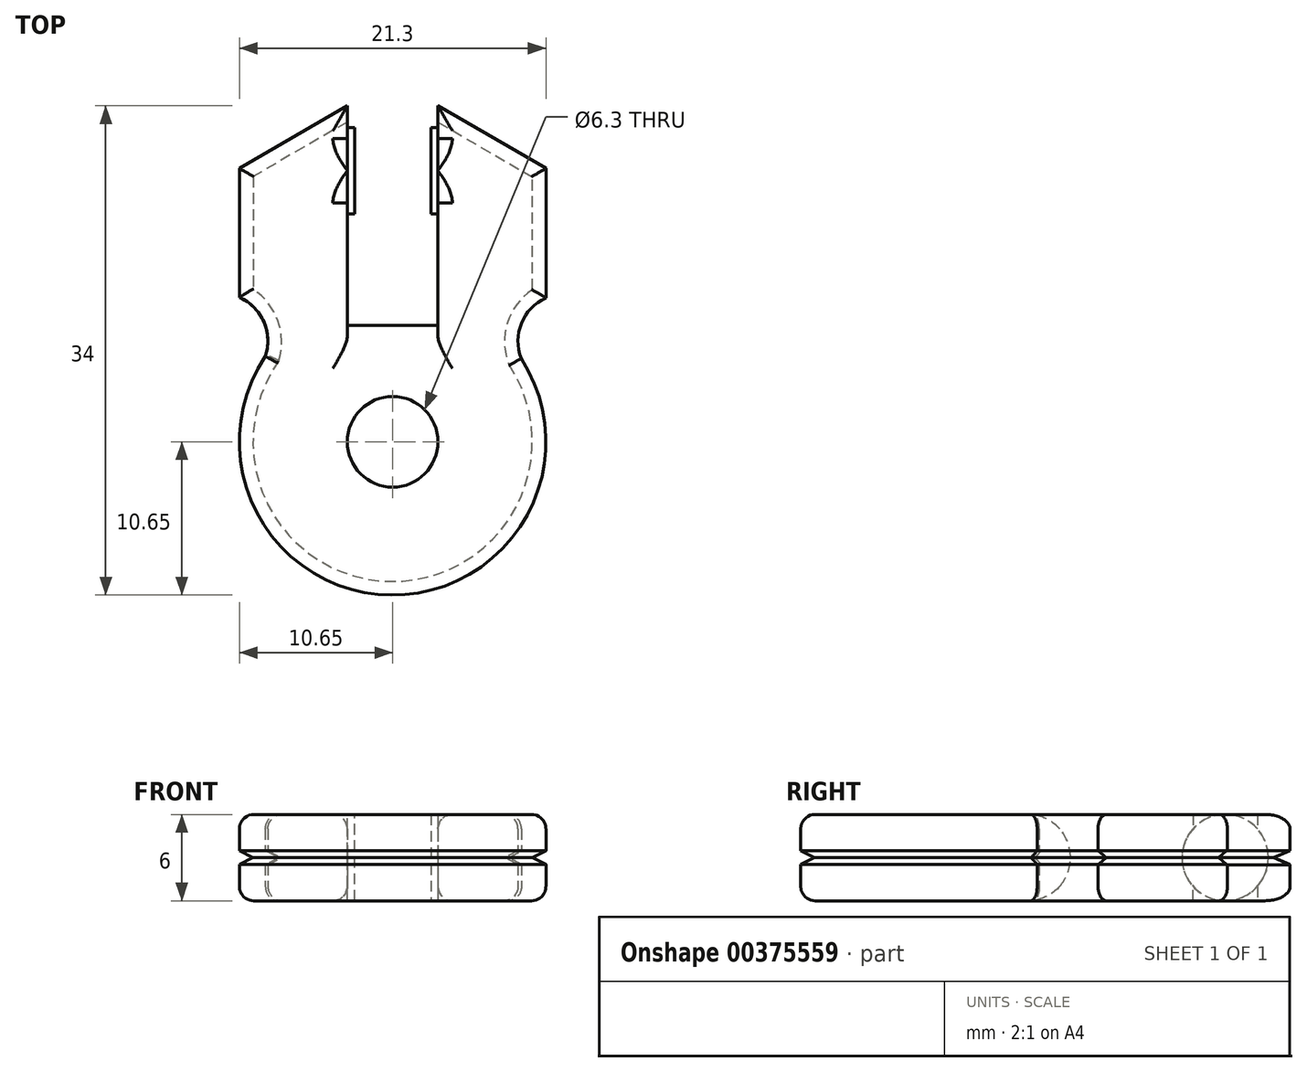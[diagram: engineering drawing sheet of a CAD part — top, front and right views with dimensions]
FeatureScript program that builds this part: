
annotation { "Feature Type Name" : "Feature", "Feature Type Description" : "" }
export const myFeature = defineFeature(function(context is Context, id is Id, definition is map)
    precondition{}
    {
        {
            var Q0;
            Q0=qCreatedBy(makeId("Top.planeOp"),FACE);
            var sketch = newSketch(context, id + "F0", { "sketchPlane" : qUnion([Q0])});
            skCircle(sketch, "E0", {"center": v(0, 0) * mm, "radius": 10.65 * mm});
            skCircle(sketch, "E1", {"center": v(0, 0) * mm, "radius": 3.15 * mm});
            skLineSegment(sketch, "E2", {"start": v(0, 0) * mm, "end": v(0, 8.1) * mm});
            skLineSegment(sketch, "E3", {"start": v(0, 8.1) * mm, "end": v(3.15, 8.1) * mm});
            skLineSegment(sketch, "E4", {"start": v(0, 8.1) * mm, "end": v(-3.15, 8.1) * mm});
            skLineSegment(sketch, "E5", {"start": v(-3.15, 8.1) * mm, "end": v(-3.15, 23.35) * mm});
            skLineSegment(sketch, "E6", {"start": v(3.15, 8.1) * mm, "end": v(3.15, 23.35) * mm});
            skLineSegment(sketch, "E7", {"start": v(10.65, 19) * mm, "end": v(3.15, 23.35) * mm});
            skLineSegment(sketch, "E8", {"start": v(10.65, 19) * mm, "end": v(10.65, 10) * mm});
            skLineSegment(sketch, "E9", {"start": v(-10.65, 19) * mm, "end": v(-3.15, 23.35) * mm});
            skLineSegment(sketch, "E10", {"start": v(-10.65, 19) * mm, "end": v(-10.65, 10) * mm});
            skLineSegment(sketch, "E11", {"start": v(0, 0) * mm, "end": v(-10.65, 0) * mm});
            skArc(sketch, "E12", {"start": v(-8.85, 5.93) * mm, "mid": v(-8.95, 8.34) * mm, "end": v(-10.65, 10.04) * mm});
            skLineSegment(sketch, "E13", {"start": v(0, 0) * mm, "end": v(10.65, 0) * mm});
            skArc(sketch, "E14", {"start": v(10.65, 10) * mm, "mid": v(8.95, 8.23) * mm, "end": v(8.94, 5.78) * mm});
            skSolve(sketch);
        }
        {
            var Q0;
            {var subQ0=sQuery(id+"F0.wireOp",EDGE,"E7");Q0=makeQuery(id+"F0.imprint","IMPRINT",FACE,{"disambiguationData":[TD([[makeQuery(id+"F0.imprint","IMPRINT",EDGE,{"derivedFrom":subQ0}),1.0]])]});}
            var Q1;
            {var subQ9=sQuery(id+"F0.wireOp",EDGE,"E3");Q1=makeQuery(id+"F0.imprint","IMPRINT",FACE,{"disambiguationData":[TD([[makeQuery(id+"F0.imprint","IMPRINT",EDGE,{"derivedFrom":subQ9}),-1.0]])]});}
            var Q2;
            {var subQ0=sQuery(id+"F0.wireOp",EDGE,"E4");Q2=makeQuery(id+"F0.imprint","IMPRINT",FACE,{"disambiguationData":[TD([[makeQuery(id+"F0.imprint","IMPRINT",EDGE,{"derivedFrom":subQ0}),1.0]])]});}
            var Q3;
            {var subQ0=sQuery(id+"F0.wireOp",EDGE,"E11");var subQ1=sQuery(id+"F0.wireOp",EDGE,"E0");var subQ2=makeQuery(id+"F0.imprint","INTERSECT",VERTEX,{"derivedFrom":[subQ1,subQ0]});Q3=makeQuery(id+"F0.imprint","IMPRINT",FACE,{"disambiguationData":[TD([[makeQuery(id+"F0.imprint","IMPRINT",EDGE,{"disambiguationData":[TD([[subQ2,-1.0]])],"derivedFrom":subQ1}),1.0]])]});}
            var Q4;
            {var subQ1=sQuery(id+"F0.wireOp",EDGE,"E9");Q4=makeQuery(id+"F0.imprint","IMPRINT",FACE,{"disambiguationData":[TD([[makeQuery(id+"F0.imprint","IMPRINT",EDGE,{"derivedFrom":subQ1}),-1.0]])]});}
            extrude(context, id + "F1", {"entities" : qUnion([Q0, Q1, Q2, Q3, Q4]), "depth" : 6 * mm});
        }
        {
            var Q0;
            Q0=makeQuery(id+"F1.opExtrude","SWEPT_FACE",FACE,{"disambiguationData":[OSD([sQuery(id+"F0.wireOp",EDGE,"E5")])]});
            var sketch = newSketch(context, id + "F2", { "sketchPlane" : qUnion([Q0])});
            skLineSegment(sketch, "E15", {"start": v(23.35, 0) * mm, "end": v(21.85, 0) * mm});
            skLineSegment(sketch, "E16", {"start": v(21.85, 0) * mm, "end": v(18.85, 0) * mm});
            skLineSegment(sketch, "E17", {"start": v(18.85, 0) * mm, "end": v(18.85, 3) * mm});
            skCircle(sketch, "E18", {"center": v(18.85, 3) * mm, "radius": 3 * mm});
            skSolve(sketch);
        }
        {
            var Q0;
            Q0=qSketchRegion(id+"F2",true);
            extrude(context, id + "F3", {"entities" : qUnion([Q0]), "operationType" : NewBodyOperationType.ADD, "depth" : .5 * mm});
        }
        {
            var Q0;
            Q0=makeQuery(id+"F1.opExtrude","SWEPT_FACE",FACE,{"disambiguationData":[OSD([sQuery(id+"F0.wireOp",EDGE,"E6")])]});
            var sketch = newSketch(context, id + "F4", { "sketchPlane" : qUnion([Q0])});
            skLineSegment(sketch, "E19", {"start": v(-23.35, 0) * mm, "end": v(-18.85, 0) * mm});
            skLineSegment(sketch, "E20", {"start": v(-18.85, 0) * mm, "end": v(-18.85, 3) * mm});
            skCircle(sketch, "E21", {"center": v(-18.85, 3) * mm, "radius": 3 * mm});
            skSolve(sketch);
        }
        {
            var Q0;
            {var subQ0=sQuery(id+"F4.wireOp",EDGE,"E21");var subQ1=sQuery(id+"F0.wireOp",EDGE,"E6");var subQ3=makeQuery(id+"F4.imprint","INTERSECT",VERTEX,{"derivedFrom":[makeQuery(id+"F1.opExtrude","CAP_EDGE",EDGE,{"disambiguationData":[OSD([subQ1])],"isStart":false}),subQ0]});Q0=makeQuery(id+"F4.imprint","IMPRINT",FACE,{"disambiguationData":[TD([[makeQuery(id+"F4.imprint","IMPRINT",EDGE,{"disambiguationData":[TD([[subQ3,-1.0]])],"derivedFrom":subQ0}),1.0]])]});}
            extrude(context, id + "F5", {"entities" : qUnion([Q0]), "operationType" : NewBodyOperationType.ADD, "depth" : .5 * mm});
        }
        {
            var Q0;
            Q0=makeQuery(id+"F1.opExtrude","CAP_EDGE",EDGE,{"disambiguationData":[OSD([sQuery(id+"F0.wireOp",EDGE,"E3"),sQuery(id+"F0.wireOp",EDGE,"E4")])],"isStart":false});
            fillet(context, id + "F6", {"entities" : qUnion([Q0]), "radius" : 3 * mm, "tangentPropagation" : true, "allowEdgeOverflow" : false});
        }
        {
            var Q0;
            Q0=makeQuery(id+"F1.opExtrude","CAP_EDGE",EDGE,{"disambiguationData":[OSD([sQuery(id+"F0.wireOp",EDGE,"E3"),sQuery(id+"F0.wireOp",EDGE,"E4")])],"isStart":true});
            fillet(context, id + "F7", {"entities" : qUnion([Q0]), "radius" : 3 * mm, "tangentPropagation" : true, "allowEdgeOverflow" : false});
        }
        {
            var Q0;
            Q0=makeQuery(id+"F1.opExtrude","CAP_EDGE",EDGE,{"disambiguationData":[OSD([sQuery(id+"F0.wireOp",EDGE,"E0")])],"isStart":false});
            var Q1;
            Q1=makeQuery(id+"F1.opExtrude","CAP_EDGE",EDGE,{"disambiguationData":[OSD([sQuery(id+"F0.wireOp",EDGE,"E12")])],"isStart":false});
            var Q2;
            Q2=makeQuery(id+"F1.opExtrude","CAP_EDGE",EDGE,{"disambiguationData":[OSD([sQuery(id+"F0.wireOp",EDGE,"E10")])],"isStart":false});
            var Q3;
            Q3=makeQuery(id+"F1.opExtrude","CAP_EDGE",EDGE,{"disambiguationData":[OSD([sQuery(id+"F0.wireOp",EDGE,"E9")])],"isStart":false});
            var Q4;
            {var subQ0=sQuery(id+"F0.wireOp",EDGE,"E5");var subQ1=sQuery(id+"F0.wireOp",EDGE,"E4");var subQ2=sQuery(id+"F0.wireOp",EDGE,"E3");Q4=makeQuery(id+"F3.boolean.opBoolean","SPLIT",EDGE,{"disambiguationData":[TD([makeQuery(id+"F1.opExtrude","SWEPT_FACE",FACE,{"disambiguationData":[OSD([subQ2,subQ1])]})])],"derivedFrom":makeQuery(id+"F1.opExtrude","CAP_EDGE",EDGE,{"disambiguationData":[OSD([subQ0])],"isStart":false})});}
            var Q5;
            {var subQ0=sQuery(id+"F0.wireOp",EDGE,"E9");var subQ1=sQuery(id+"F0.wireOp",EDGE,"E5");Q5=makeQuery(id+"F3.boolean.opBoolean","SPLIT",EDGE,{"disambiguationData":[TD([makeQuery(id+"F1.opExtrude","SWEPT_FACE",FACE,{"disambiguationData":[OSD([subQ0])]})])],"derivedFrom":makeQuery(id+"F1.opExtrude","CAP_EDGE",EDGE,{"disambiguationData":[OSD([subQ1])],"isStart":false})});}
            var Q6;
            {var subQ0=sQuery(id+"F0.wireOp",EDGE,"E6");var subQ1=sQuery(id+"F0.wireOp",EDGE,"E4");var subQ2=sQuery(id+"F0.wireOp",EDGE,"E3");Q6=makeQuery(id+"F5.boolean.opBoolean","SPLIT",EDGE,{"disambiguationData":[TD([makeQuery(id+"F1.opExtrude","SWEPT_FACE",FACE,{"disambiguationData":[OSD([subQ2,subQ1])]})])],"derivedFrom":makeQuery(id+"F1.opExtrude","CAP_EDGE",EDGE,{"disambiguationData":[OSD([subQ0])],"isStart":false})});}
            var Q7;
            {var subQ0=sQuery(id+"F0.wireOp",EDGE,"E7");var subQ1=sQuery(id+"F0.wireOp",EDGE,"E6");Q7=makeQuery(id+"F5.boolean.opBoolean","SPLIT",EDGE,{"disambiguationData":[TD([makeQuery(id+"F1.opExtrude","SWEPT_FACE",FACE,{"disambiguationData":[OSD([subQ0])]})])],"derivedFrom":makeQuery(id+"F1.opExtrude","CAP_EDGE",EDGE,{"disambiguationData":[OSD([subQ1])],"isStart":false})});}
            var Q8;
            Q8=makeQuery(id+"F1.opExtrude","CAP_EDGE",EDGE,{"disambiguationData":[OSD([sQuery(id+"F0.wireOp",EDGE,"E7")])],"isStart":false});
            var Q9;
            Q9=makeQuery(id+"F1.opExtrude","CAP_EDGE",EDGE,{"disambiguationData":[OSD([sQuery(id+"F0.wireOp",EDGE,"E8")])],"isStart":false});
            var Q10;
            Q10=makeQuery(id+"F1.opExtrude","CAP_EDGE",EDGE,{"disambiguationData":[OSD([sQuery(id+"F0.wireOp",EDGE,"E14")])],"isStart":false});
            var Q11;
            Q11=makeQuery(id+"F1.opExtrude","CAP_EDGE",EDGE,{"disambiguationData":[OSD([sQuery(id+"F0.wireOp",EDGE,"E0")])],"isStart":true});
            var Q12;
            Q12=makeQuery(id+"F1.opExtrude","CAP_EDGE",EDGE,{"disambiguationData":[OSD([sQuery(id+"F0.wireOp",EDGE,"E10")])],"isStart":true});
            var Q13;
            Q13=makeQuery(id+"F1.opExtrude","CAP_EDGE",EDGE,{"disambiguationData":[OSD([sQuery(id+"F0.wireOp",EDGE,"E12")])],"isStart":true});
            var Q14;
            Q14=makeQuery(id+"F1.opExtrude","CAP_EDGE",EDGE,{"disambiguationData":[OSD([sQuery(id+"F0.wireOp",EDGE,"E9")])],"isStart":true});
            var Q15;
            {var subQ0=sQuery(id+"F0.wireOp",EDGE,"E6");var subQ1=sQuery(id+"F0.wireOp",EDGE,"E4");var subQ2=sQuery(id+"F0.wireOp",EDGE,"E3");Q15=makeQuery(id+"F5.boolean.opBoolean","SPLIT",EDGE,{"disambiguationData":[TD([makeQuery(id+"F1.opExtrude","SWEPT_FACE",FACE,{"disambiguationData":[OSD([subQ2,subQ1])]})])],"derivedFrom":makeQuery(id+"F1.opExtrude","CAP_EDGE",EDGE,{"disambiguationData":[OSD([subQ0])],"isStart":true})});}
            var Q16;
            {var subQ0=sQuery(id+"F0.wireOp",EDGE,"E5");var subQ1=sQuery(id+"F0.wireOp",EDGE,"E4");var subQ2=sQuery(id+"F0.wireOp",EDGE,"E3");Q16=makeQuery(id+"F3.boolean.opBoolean","SPLIT",EDGE,{"disambiguationData":[TD([makeQuery(id+"F1.opExtrude","SWEPT_FACE",FACE,{"disambiguationData":[OSD([subQ2,subQ1])]})])],"derivedFrom":makeQuery(id+"F1.opExtrude","CAP_EDGE",EDGE,{"disambiguationData":[OSD([subQ0])],"isStart":true})});}
            var Q17;
            {var subQ0=sQuery(id+"F0.wireOp",EDGE,"E9");var subQ1=sQuery(id+"F0.wireOp",EDGE,"E5");Q17=makeQuery(id+"F3.boolean.opBoolean","SPLIT",EDGE,{"disambiguationData":[TD([makeQuery(id+"F1.opExtrude","SWEPT_FACE",FACE,{"disambiguationData":[OSD([subQ0])]})])],"derivedFrom":makeQuery(id+"F1.opExtrude","CAP_EDGE",EDGE,{"disambiguationData":[OSD([subQ1])],"isStart":true})});}
            var Q18;
            Q18=makeQuery(id+"F1.opExtrude","CAP_EDGE",EDGE,{"disambiguationData":[OSD([sQuery(id+"F0.wireOp",EDGE,"E7")])],"isStart":true});
            var Q19;
            Q19=makeQuery(id+"F1.opExtrude","CAP_EDGE",EDGE,{"disambiguationData":[OSD([sQuery(id+"F0.wireOp",EDGE,"E8")])],"isStart":true});
            var Q20;
            Q20=makeQuery(id+"F1.opExtrude","CAP_EDGE",EDGE,{"disambiguationData":[OSD([sQuery(id+"F0.wireOp",EDGE,"E14")])],"isStart":true});
            var Q21;
            {var subQ0=sQuery(id+"F0.wireOp",EDGE,"E7");var subQ1=sQuery(id+"F0.wireOp",EDGE,"E6");Q21=makeQuery(id+"F5.boolean.opBoolean","SPLIT",EDGE,{"disambiguationData":[TD([makeQuery(id+"F1.opExtrude","SWEPT_FACE",FACE,{"disambiguationData":[OSD([subQ0])]})])],"derivedFrom":makeQuery(id+"F1.opExtrude","CAP_EDGE",EDGE,{"disambiguationData":[OSD([subQ1])],"isStart":true})});}
            fillet(context, id + "F8", {"entities" : qUnion([Q0, Q1, Q2, Q3, Q4, Q5, Q6, Q7, Q8, Q9, Q10, Q11, Q12, Q13, Q14, Q15, Q16, Q17, Q18, Q19, Q20, Q21]), "radius" : 1 * mm, "tangentPropagation" : true, "allowEdgeOverflow" : false});
        }
        {
            var Q0;
            Q0=qCreatedBy(makeId("Top.planeOp"),FACE);
            cPlane(context, id + "F9", {"entities" : qUnion([Q0]), "cplaneType" : CPlaneType.OFFSET, "offset" : 3 * mm, "width" : 150 * mm, "height" : 150 * mm});
        }
        {
            var Q0;
            Q0=qCreatedBy(id+"F9.planeOp",FACE);
            var sketch = newSketch(context, id + "F10", { "sketchPlane" : qUnion([Q0])});
            skLineSegment(sketch, "E22", {"start": v(10.72, 18.98) * mm, "end": v(3.22, 23.33) * mm});
            skLineSegment(sketch, "E23", {"start": v(10.72, 18.98) * mm, "end": v(10.72, 9.98) * mm});
            skLineSegment(sketch, "E24", {"start": v(-10.68, 19.02) * mm, "end": v(-3.18, 23.37) * mm});
            skLineSegment(sketch, "E25", {"start": v(-10.68, 19.02) * mm, "end": v(-10.68, 10.02) * mm});
            skArc(sketch, "E26", {"start": v(-10.68, 0.76) * mm, "mid": v(-10.68, 0.76) * mm, "end": v(-10.68, 0.76) * mm});
            skArc(sketch, "E27", {"start": v(-8.82, 6.07) * mm, "mid": v(-0.15, -10.7) * mm, "end": v(8.99, 5.81) * mm});
            skArc(sketch, "E28", {"start": v(-8.82, 6.07) * mm, "mid": v(-9.04, 8.38) * mm, "end": v(-10.68, 10.02) * mm});
            skArc(sketch, "E29", {"start": v(10.72, 9.98) * mm, "mid": v(9.02, 8.24) * mm, "end": v(8.99, 5.81) * mm});
            skLineSegment(sketch, "E30", {"start": v(3.22, 23.33) * mm, "end": v(3.14, 23.37) * mm});
            skLineSegment(sketch, "E31", {"start": v(3.14, 23.37) * mm, "end": v(-3.18, 23.37) * mm});
            skLineSegment(sketch, "E32.0", {"start": v(9.72, 18.4) * mm, "end": v(9.72, 10.57) * mm});
            skArc(sketch, "E32.1", {"start": v(9.72, 10.57) * mm, "mid": v(7.96, 8.25) * mm, "end": v(8.1, 5.35) * mm});
            skLineSegment(sketch, "E32.2", {"start": v(9.72, 18.4) * mm, "end": v(2.87, 22.37) * mm});
            skArc(sketch, "E32.3", {"start": v(-7.9, 5.63) * mm, "mid": v(-0.17, -9.7) * mm, "end": v(8.1, 5.35) * mm});
            skLineSegment(sketch, "E32.4", {"start": v(2.87, 22.37) * mm, "end": v(-2.9, 22.37) * mm});
            skLineSegment(sketch, "E32.5", {"start": v(-9.68, 18.44) * mm, "end": v(-2.9, 22.37) * mm});
            skLineSegment(sketch, "E32.6", {"start": v(-9.68, 18.44) * mm, "end": v(-9.68, 10.6) * mm});
            skArc(sketch, "E32.7", {"start": v(-7.9, 5.63) * mm, "mid": v(-7.97, 8.4) * mm, "end": v(-9.68, 10.6) * mm});
            skSolve(sketch);
        }
        {
            var Q0;
            Q0 = qSketchRegion(id + "F10", true);
            extrude(context, id + "F11", {"entities" : qUnion([Q0]), "operationType" : NewBodyOperationType.REMOVE, "depth" : .5 * mm, "hasSecondDirection" : true, "secondDirectionOppositeDirection" : true, "secondDirectionDepth" : .5 * mm});
        }
        {
            var Q0;
            Q0=makeQuery(id+"F11.boolean.opBoolean","COPY",EDGE,{"derivedFrom":makeQuery(id+"F11.opExtrude","CAP_EDGE",EDGE,{"disambiguationData":[OSD([sQuery(id+"F10.wireOp",EDGE,"E32.5")])],"isStart":true})});
            var Q1;
            Q1=makeQuery(id+"F11.boolean.opBoolean","COPY",EDGE,{"derivedFrom":makeQuery(id+"F11.opExtrude","CAP_EDGE",EDGE,{"disambiguationData":[OSD([sQuery(id+"F10.wireOp",EDGE,"E32.5")])],"isStart":false})});
            var Q2;
            Q2=makeQuery(id+"F11.boolean.opBoolean","COPY",EDGE,{"derivedFrom":makeQuery(id+"F11.opExtrude","CAP_EDGE",EDGE,{"disambiguationData":[OSD([sQuery(id+"F10.wireOp",EDGE,"E32.6")])],"isStart":true})});
            var Q3;
            Q3=makeQuery(id+"F11.boolean.opBoolean","COPY",EDGE,{"derivedFrom":makeQuery(id+"F11.opExtrude","CAP_EDGE",EDGE,{"disambiguationData":[OSD([sQuery(id+"F10.wireOp",EDGE,"E32.6")])],"isStart":false})});
            var Q4;
            Q4=makeQuery(id+"F11.boolean.opBoolean","COPY",EDGE,{"derivedFrom":makeQuery(id+"F11.opExtrude","CAP_EDGE",EDGE,{"disambiguationData":[OSD([sQuery(id+"F10.wireOp",EDGE,"E32.3")])],"isStart":true})});
            var Q5;
            Q5=makeQuery(id+"F11.boolean.opBoolean","COPY",EDGE,{"derivedFrom":makeQuery(id+"F11.opExtrude","CAP_EDGE",EDGE,{"disambiguationData":[OSD([sQuery(id+"F10.wireOp",EDGE,"E32.3")])],"isStart":false})});
            var Q6;
            Q6=makeQuery(id+"F11.boolean.opBoolean","COPY",EDGE,{"derivedFrom":makeQuery(id+"F11.opExtrude","CAP_EDGE",EDGE,{"disambiguationData":[OSD([sQuery(id+"F10.wireOp",EDGE,"E32.2")])],"isStart":false})});
            var Q7;
            Q7=makeQuery(id+"F11.boolean.opBoolean","COPY",EDGE,{"derivedFrom":makeQuery(id+"F11.opExtrude","CAP_EDGE",EDGE,{"disambiguationData":[OSD([sQuery(id+"F10.wireOp",EDGE,"E32.2")])],"isStart":true})});
            var Q8;
            Q8=makeQuery(id+"F11.boolean.opBoolean","COPY",EDGE,{"derivedFrom":makeQuery(id+"F11.opExtrude","CAP_EDGE",EDGE,{"disambiguationData":[OSD([sQuery(id+"F10.wireOp",EDGE,"E32.0")])],"isStart":true})});
            chamfer(context, id + "F12", {"entities" : qUnion([Q0, Q1, Q2, Q3, Q4, Q5, Q6, Q7, Q8]), "chamferType" : ChamferType.TWO_OFFSETS, "width1" : 1 * mm, "oppositeDirection" : false, "width2" : .5 * mm, "tangentPropagation" : true});
        }
        {
            var Q0;
            Q0=makeQuery(id+"F11.boolean.opBoolean","COPY",EDGE,{"derivedFrom":makeQuery(id+"F11.opExtrude","CAP_EDGE",EDGE,{"disambiguationData":[OSD([sQuery(id+"F10.wireOp",EDGE,"E32.0")])],"isStart":false})});
            var Q1;
            Q1=makeQuery(id+"F11.boolean.opBoolean","COPY",EDGE,{"derivedFrom":makeQuery(id+"F11.opExtrude","CAP_EDGE",EDGE,{"disambiguationData":[OSD([sQuery(id+"F10.wireOp",EDGE,"E32.1")])],"isStart":false})});
            var Q2;
            Q2=makeQuery(id+"F11.boolean.opBoolean","COPY",EDGE,{"derivedFrom":makeQuery(id+"F11.opExtrude","CAP_EDGE",EDGE,{"disambiguationData":[OSD([sQuery(id+"F10.wireOp",EDGE,"E32.7")])],"isStart":false})});
            chamfer(context, id + "F13", {"entities" : qUnion([Q0, Q1, Q2]), "chamferType" : ChamferType.TWO_OFFSETS, "width1" : .5 * mm, "oppositeDirection" : false, "width2" : 1 * mm, "tangentPropagation" : true});
        }
        {
            var Q0;
            Q0=makeQuery(id+"F11.boolean.opBoolean","COPY",EDGE,{"derivedFrom":makeQuery(id+"F11.opExtrude","CAP_EDGE",EDGE,{"disambiguationData":[OSD([sQuery(id+"F10.wireOp",EDGE,"E32.1")])],"isStart":true})});
            var Q1;
            Q1=makeQuery(id+"F11.boolean.opBoolean","COPY",EDGE,{"derivedFrom":makeQuery(id+"F11.opExtrude","CAP_EDGE",EDGE,{"disambiguationData":[OSD([sQuery(id+"F10.wireOp",EDGE,"E32.7")])],"isStart":true})});
            chamfer(context, id + "F14", {"entities" : qUnion([Q0, Q1]), "chamferType" : ChamferType.TWO_OFFSETS, "width1" : 1 * mm, "oppositeDirection" : false, "width2" : .5 * mm, "tangentPropagation" : true});
        }
    });
